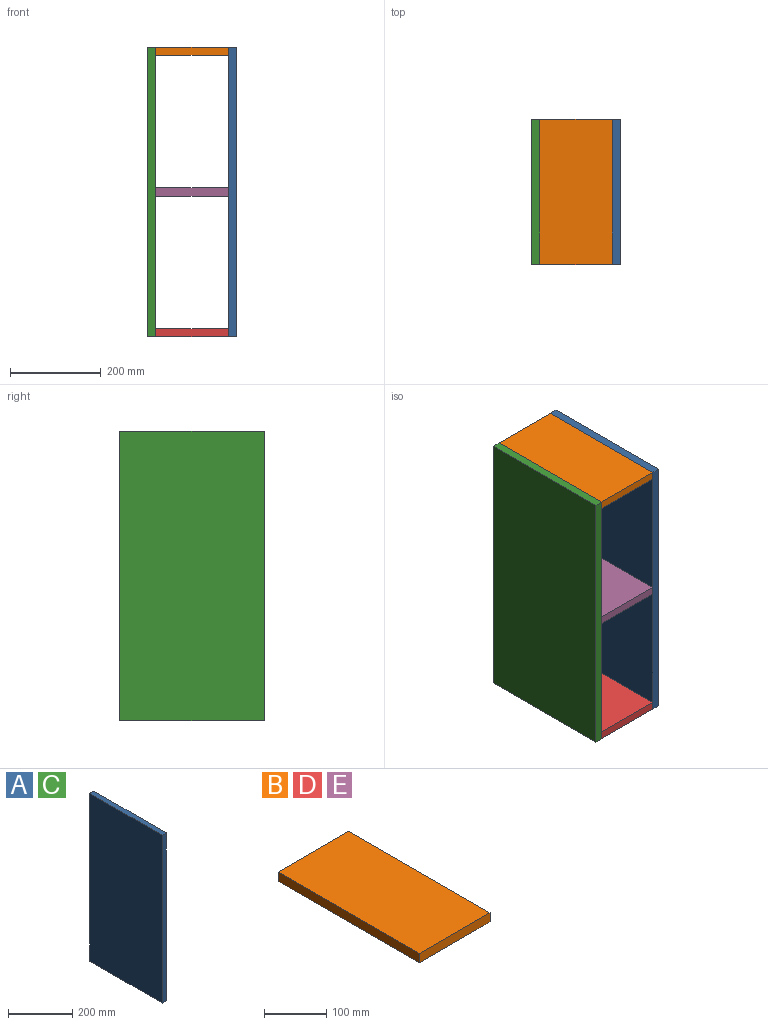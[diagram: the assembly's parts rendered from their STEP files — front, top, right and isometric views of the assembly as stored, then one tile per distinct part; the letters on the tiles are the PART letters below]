
ASSEMBLY  parts=5 mates=4
PART A: 6 faces, bbox 18x320x640 mm
  f0: plane 320x18mm, normal (0,0,1), area 5760mm2, adj f1,f3,f4,f5
  f1: plane 640x18mm, normal (0,-1,0), area 11520mm2, adj f0,f2,f4,f5
  f2: plane 320x18mm, normal (0,0,-1), area 5760mm2, adj f1,f3,f4,f5
  f3: plane 640x18mm, normal (0,1,0), area 11520mm2, adj f0,f2,f4,f5
  f4: plane 640x320mm, normal (1,0,0), area 204800mm2, adj f0,f1,f2,f3
  f5: plane 640x320mm, normal (-1,0,0), area 204800mm2, adj f0,f1,f2,f3
PART B: 6 faces, bbox 160x320x18 mm
  f0: plane 320x18mm, normal (1,0,0), area 5760mm2, adj f1,f3,f4,f5
  f1: plane 160x18mm, normal (0,1,0), area 2880mm2, adj f0,f2,f4,f5
  f2: plane 320x18mm, normal (-1,0,0), area 5760mm2, adj f1,f3,f4,f5
  f3: plane 160x18mm, normal (0,-1,0), area 2880mm2, adj f0,f2,f4,f5
  f4: plane 320x160mm, normal (0,0,1), area 51200mm2, adj f0,f1,f2,f3
  f5: plane 320x160mm, normal (0,0,-1), area 51200mm2, adj f0,f1,f2,f3
PART C: same geometry as A
PART D: same geometry as B
PART E: same geometry as B
PLACE A t=(41.39,-32.92,157.7)mm
PLACE B t=(41.39,-32.92,139.7)mm
PLACE C t=(-136.61,-32.92,157.7)mm
PLACE D t=(41.39,-32.92,-482.3)mm
PLACE E t=(41.39,-32.92,-171.3)mm
MATE fastened B.f0 <-> A.f5  axis (1,0,0) through (121.39,-192.92,157.7)mm
MATE fastened D.f2 <-> C.f4  axis (-1,0,0) through (-38.61,-192.92,-482.3)mm
MATE fastened C.f4 <-> B.f2  axis (1,0,0) through (-38.61,-192.92,157.7)mm
MATE fastened E.f0 <-> A.f5  axis (1,0,0) through (121.39,-192.92,-162.3)mm
